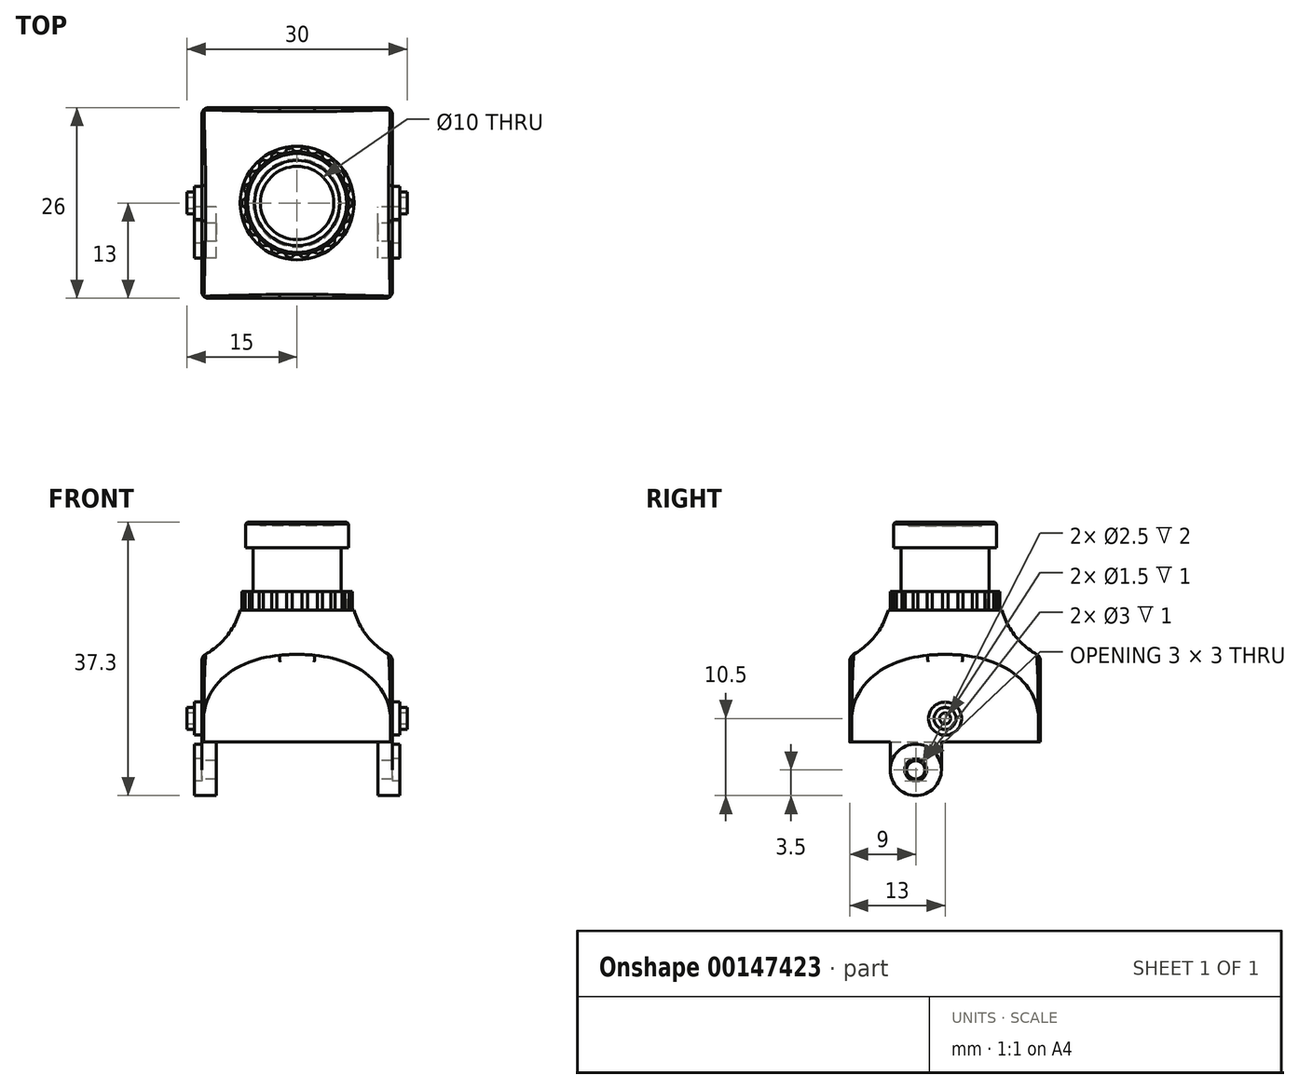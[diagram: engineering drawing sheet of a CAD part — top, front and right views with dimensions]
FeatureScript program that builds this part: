
annotation { "Feature Type Name" : "Feature", "Feature Type Description" : "" }
export const myFeature = defineFeature(function(context is Context, id is Id, definition is map)
    precondition{}
    {
        {
            var Q0;
            Q0=qCreatedBy(makeId("Front.planeOp"),FACE);
            var sketch = newSketch(context, id + "F0", { "sketchPlane" : qUnion([Q0])});
            skLineSegment(sketch, "E0", {"start": v(0, 83.46) * mm, "end": v(0, 0) * mm, "construction": true});
            skLineSegment(sketch, "E1", {"start": v(5, 30) * mm, "end": v(7, 30) * mm});
            skLineSegment(sketch, "E2", {"start": v(7, 30) * mm, "end": v(7, 26.5) * mm});
            skLineSegment(sketch, "E3", {"start": v(7, 26.5) * mm, "end": v(6, 26.5) * mm});
            skLineSegment(sketch, "E4", {"start": v(6, 26.5) * mm, "end": v(6, 20.5) * mm});
            skLineSegment(sketch, "E5", {"start": v(6, 20.5) * mm, "end": v(7.5, 20.5) * mm});
            skLineSegment(sketch, "E6", {"start": v(7.5, 20.5) * mm, "end": v(7.5, 18) * mm});
            skLineSegment(sketch, "E7", {"start": v(7.75, 18) * mm, "end": v(7.5, 18) * mm});
            skLineSegment(sketch, "E8", {"start": v(18, 3) * mm, "end": v(18, 0) * mm});
            skLineSegment(sketch, "E9", {"start": v(18, 0) * mm, "end": v(0, 0) * mm});
            skArc(sketch, "E10", {"start": v(7.75, 18) * mm, "mid": v(9.59, 14.4) * mm, "end": v(12.7, 11.83) * mm});
            skArc(sketch, "E11", {"start": v(18, 3) * mm, "mid": v(16.57, 8.15) * mm, "end": v(12.7, 11.83) * mm});
            skLineSegment(sketch, "E12", {"start": v(5, 30) * mm, "end": v(5, 29.5) * mm});
            skLineSegment(sketch, "E13", {"start": v(0, 29.36) * mm, "end": v(0, 0) * mm});
            skLineSegment(sketch, "E14", {"start": v(0, 29.86) * mm, "end": v(0, 29.36) * mm});
            skArc(sketch, "E15", {"start": v(5, 29.5) * mm, "mid": v(2.5, 29.77) * mm, "end": v(0, 29.86) * mm});
            skSolve(sketch);
        }
        {
            var Q0;
            Q0=makeQuery(id+"F0.imprint","IMPRINT",FACE,{"disambiguationData":[TD([[makeQuery(id+"F0.imprint","IMPRINT",EDGE,{"derivedFrom":sQuery(id+"F0.wireOp",EDGE,"E1")}),-1.0]])]});
            var Q1;
            Q1=sQuery(id+"F0.wireOp",EDGE,"E0");
            revolve(context, id + "F1", {"entities" : qUnion([Q0]), "axis" : qUnion([Q1]), "revolveType" : RevolveType.FULL});
        }
        {
            var Q0;
            Q0=makeQuery(id+"F1.opRevolve","SWEPT_FACE",FACE,{"disambiguationData":[OSD([sQuery(id+"F0.wireOp",EDGE,"E9")])]});
            var sketch = newSketch(context, id + "F2", { "sketchPlane" : qUnion([Q0])});
            skLineSegment(sketch, "E16.bottom", {"start": v(-13, 13) * mm, "end": v(13, 13) * mm});
            skLineSegment(sketch, "E16.top", {"start": v(-13, -13) * mm, "end": v(13, -13) * mm});
            skLineSegment(sketch, "E16.left", {"start": v(-13, 13) * mm, "end": v(-13, -13) * mm});
            skLineSegment(sketch, "E16.right", {"start": v(13, 13) * mm, "end": v(13, -13) * mm});
            skCircle(sketch, "E17", {"center": v(0, 0) * mm, "radius": 20 * mm});
            skSolve(sketch);
        }
        {
            var Q0;
            Q0=qSketchRegion(id+"F2",true);
            extrude(context, id + "F3", {"entities" : qUnion([Q0]), "operationType" : NewBodyOperationType.REMOVE, "oppositeDirection" : true, "depth" : 15 * mm});
        }
        {
            var Q0;
            Q0=makeQuery(id+"F3.boolean.opBoolean","INTERSECT",EDGE,{"disambiguationData":[OD(1.0)],"derivedFrom":[makeQuery(id+"F1.opRevolve","SWEPT_FACE",FACE,{"disambiguationData":[OSD([sQuery(id+"F0.wireOp",EDGE,"E8")])]}),makeQuery(id+"F3.opExtrude","SWEPT_FACE",FACE,{"disambiguationData":[OSD([sQuery(id+"F2.wireOp",EDGE,"E16.left")])]})]});
            var Q1;
            Q1=makeQuery(id+"F3.boolean.opBoolean","INTERSECT",EDGE,{"disambiguationData":[OD(1.0)],"derivedFrom":[makeQuery(id+"F1.opRevolve","SWEPT_FACE",FACE,{"disambiguationData":[OSD([sQuery(id+"F0.wireOp",EDGE,"E11")])]}),makeQuery(id+"F3.opExtrude","SWEPT_FACE",FACE,{"disambiguationData":[OSD([sQuery(id+"F2.wireOp",EDGE,"E16.left")])]})]});
            var Q2;
            Q2=makeQuery(id+"F3.boolean.opBoolean","INTERSECT",EDGE,{"derivedFrom":[makeQuery(id+"F1.opRevolve","SWEPT_FACE",FACE,{"disambiguationData":[OSD([sQuery(id+"F0.wireOp",EDGE,"E10")])]}),makeQuery(id+"F3.opExtrude","SWEPT_FACE",FACE,{"disambiguationData":[OSD([sQuery(id+"F2.wireOp",EDGE,"E16.left")])]})]});
            var Q3;
            Q3=makeQuery(id+"F3.boolean.opBoolean","INTERSECT",EDGE,{"disambiguationData":[OD(0.0)],"derivedFrom":[makeQuery(id+"F1.opRevolve","SWEPT_FACE",FACE,{"disambiguationData":[OSD([sQuery(id+"F0.wireOp",EDGE,"E11")])]}),makeQuery(id+"F3.opExtrude","SWEPT_FACE",FACE,{"disambiguationData":[OSD([sQuery(id+"F2.wireOp",EDGE,"E16.left")])]})]});
            var Q4;
            Q4=makeQuery(id+"F3.boolean.opBoolean","INTERSECT",EDGE,{"disambiguationData":[OD(0.0)],"derivedFrom":[makeQuery(id+"F1.opRevolve","SWEPT_FACE",FACE,{"disambiguationData":[OSD([sQuery(id+"F0.wireOp",EDGE,"E8")])]}),makeQuery(id+"F3.opExtrude","SWEPT_FACE",FACE,{"disambiguationData":[OSD([sQuery(id+"F2.wireOp",EDGE,"E16.left")])]})]});
            var Q5;
            Q5=makeQuery(id+"F3.boolean.opBoolean","INTERSECT",EDGE,{"disambiguationData":[OD(0.0)],"derivedFrom":[makeQuery(id+"F1.opRevolve","SWEPT_FACE",FACE,{"disambiguationData":[OSD([sQuery(id+"F0.wireOp",EDGE,"E8")])]}),makeQuery(id+"F3.opExtrude","SWEPT_FACE",FACE,{"disambiguationData":[OSD([sQuery(id+"F2.wireOp",EDGE,"E16.top")])]})]});
            var Q6;
            Q6=makeQuery(id+"F3.boolean.opBoolean","INTERSECT",EDGE,{"disambiguationData":[OD(1.0)],"derivedFrom":[makeQuery(id+"F1.opRevolve","SWEPT_FACE",FACE,{"disambiguationData":[OSD([sQuery(id+"F0.wireOp",EDGE,"E8")])]}),makeQuery(id+"F3.opExtrude","SWEPT_FACE",FACE,{"disambiguationData":[OSD([sQuery(id+"F2.wireOp",EDGE,"E16.right")])]})]});
            var Q7;
            Q7=makeQuery(id+"F3.boolean.opBoolean","INTERSECT",EDGE,{"disambiguationData":[OD(1.0)],"derivedFrom":[makeQuery(id+"F1.opRevolve","SWEPT_FACE",FACE,{"disambiguationData":[OSD([sQuery(id+"F0.wireOp",EDGE,"E8")])]}),makeQuery(id+"F3.opExtrude","SWEPT_FACE",FACE,{"disambiguationData":[OSD([sQuery(id+"F2.wireOp",EDGE,"E16.bottom")])]})]});
            fillet(context, id + "F4", {"entities" : qUnion([Q0, Q1, Q2, Q3, Q4, Q5, Q6, Q7]), "radius" : 1 * mm, "tangentPropagation" : true, "allowEdgeOverflow" : false});
        }
        {
            var Q0;
            Q0=makeQuery(id+"F1.opRevolve","SWEPT_FACE",FACE,{"disambiguationData":[OSD([sQuery(id+"F0.wireOp",EDGE,"E5")])]});
            var sketch = newSketch(context, id + "F5", { "sketchPlane" : qUnion([Q0])});
            skCircle(sketch, "E18", {"center": v(0, 7.75) * mm, "radius": 0.75 * mm});
            skCircle(sketch, "E19.1.0", {"center": v(-2.18, 7.44) * mm, "radius": 0.75 * mm});
            skCircle(sketch, "E19.2.0", {"center": v(-4.19, 6.52) * mm, "radius": 0.75 * mm});
            skCircle(sketch, "E19.3.0", {"center": v(-5.86, 5.08) * mm, "radius": 0.75 * mm});
            skCircle(sketch, "E19.4.0", {"center": v(-7.05, 3.22) * mm, "radius": 0.75 * mm});
            skCircle(sketch, "E19.5.0", {"center": v(-7.67, 1.1) * mm, "radius": 0.75 * mm});
            skCircle(sketch, "E19.6.0", {"center": v(-7.67, -1.1) * mm, "radius": 0.75 * mm});
            skCircle(sketch, "E19.7.0", {"center": v(-7.05, -3.22) * mm, "radius": 0.75 * mm});
            skCircle(sketch, "E19.8.0", {"center": v(-5.86, -5.08) * mm, "radius": 0.75 * mm});
            skCircle(sketch, "E19.9.0", {"center": v(-4.19, -6.52) * mm, "radius": 0.75 * mm});
            skCircle(sketch, "E19.10.0", {"center": v(-2.18, -7.44) * mm, "radius": 0.75 * mm});
            skCircle(sketch, "E19.11.0", {"center": v(0, -7.75) * mm, "radius": 0.75 * mm});
            skCircle(sketch, "E19.12.0", {"center": v(2.18, -7.44) * mm, "radius": 0.75 * mm});
            skCircle(sketch, "E19.13.0", {"center": v(4.19, -6.52) * mm, "radius": 0.75 * mm});
            skCircle(sketch, "E19.14.0", {"center": v(5.86, -5.08) * mm, "radius": 0.75 * mm});
            skCircle(sketch, "E19.15.0", {"center": v(7.05, -3.22) * mm, "radius": 0.75 * mm});
            skCircle(sketch, "E19.16.0", {"center": v(7.67, -1.1) * mm, "radius": 0.75 * mm});
            skCircle(sketch, "E19.17.0", {"center": v(7.67, 1.1) * mm, "radius": 0.75 * mm});
            skCircle(sketch, "E19.18.0", {"center": v(7.05, 3.22) * mm, "radius": 0.75 * mm});
            skCircle(sketch, "E19.19.0", {"center": v(5.86, 5.08) * mm, "radius": 0.75 * mm});
            skCircle(sketch, "E19.20.0", {"center": v(4.19, 6.52) * mm, "radius": 0.75 * mm});
            skCircle(sketch, "E19.21.0", {"center": v(2.18, 7.44) * mm, "radius": 0.75 * mm});
            skPoint(sketch, "E19.center", {"position": v(0, 0) * mm});
            skCircle(sketch, "E20", {"center": v(0, 0) * mm, "radius": 7.75 * mm, "construction": true});
            skLineSegment(sketch, "E21", {"start": v(0, 7.75) * mm, "end": v(0, 0) * mm, "construction": true});
            skLineSegment(sketch, "E22", {"start": v(0, 0) * mm, "end": v(2.18, 7.44) * mm, "construction": true});
            skSolve(sketch);
        }
        {
            var Q0;
            Q0=qSketchRegion(id+"F5",true);
            extrude(context, id + "F6", {"entities" : qUnion([Q0]), "operationType" : NewBodyOperationType.REMOVE, "oppositeDirection" : true, "depth" : 2.5 * mm});
        }
        {
            var Q0;
            Q0=makeQuery(id+"F1.opRevolve","SWEPT_EDGE",EDGE,{"disambiguationData":[OSD([sQuery(id+"F0.wireOp",EDGE,"E1"),sQuery(id+"F0.wireOp",EDGE,"E2")])]});
            chamfer(context, id + "F7", {"entities" : qUnion([Q0]), "width" : 0.25 * mm, "tangentPropagation" : true});
        }
        {
            var Q0;
            Q0=makeQuery(id+"F1.opRevolve","SWEPT_EDGE",EDGE,{"disambiguationData":[OSD([sQuery(id+"F0.wireOp",EDGE,"E1"),sQuery(id+"F0.wireOp",EDGE,"E12")])]});
            chamfer(context, id + "F8", {"entities" : qUnion([Q0]), "chamferType" : ChamferType.TWO_OFFSETS, "width1" : 0.4 * mm, "oppositeDirection" : false, "width2" : 0.8 * mm, "tangentPropagation" : true});
        }
        {
            var Q0;
            Q0=qCreatedBy(makeId("Right.planeOp"),FACE);
            var sketch = newSketch(context, id + "F9", { "sketchPlane" : qUnion([Q0])});
            skCircle(sketch, "E23", {"center": v(0, 3.2) * mm, "radius": 2.25 * mm});
            skSolve(sketch);
        }
        {
            var Q0;
            Q0=qSketchRegion(id+"F9",true);
            extrude(context, id + "F10", {"entities" : qUnion([Q0]), "operationType" : NewBodyOperationType.ADD, "endBound" : BoundingType.SYMMETRIC, "depth" : 28 * mm});
        }
        {
            var Q0;
            Q0=qCreatedBy(makeId("Right.planeOp"),FACE);
            var sketch = newSketch(context, id + "F11", { "sketchPlane" : qUnion([Q0])});
            skCircle(sketch, "E24", {"center": v(0, 3.2) * mm, "radius": 1.5 * mm});
            skCircle(sketch, "E25", {"center": v(0, 3.2) * mm, "radius": 0.75 * mm});
            skSolve(sketch);
        }
        {
            var Q0;
            Q0=qSketchRegion(id+"F11",true);
            extrude(context, id + "F12", {"entities" : qUnion([Q0]), "operationType" : NewBodyOperationType.ADD, "endBound" : BoundingType.SYMMETRIC, "depth" : 30 * mm});
        }
        {
            var Q0;
            Q0=qCreatedBy(makeId("Right.planeOp"),FACE);
            var sketch = newSketch(context, id + "F13", { "sketchPlane" : qUnion([Q0])});
            skLineSegment(sketch, "E26.bottom", {"start": v(-7.5, 0) * mm, "end": v(-0.5, 0) * mm});
            skLineSegment(sketch, "E26.left", {"start": v(-7.5, 0) * mm, "end": v(-7.5, -3.8) * mm});
            skLineSegment(sketch, "E26.right", {"start": v(-0.5, 0) * mm, "end": v(-0.5, -3.8) * mm});
            skArc(sketch, "E27", {"start": v(-7.5, -3.8) * mm, "mid": v(-4, -7.3) * mm, "end": v(-0.5, -3.8) * mm});
            skCircle(sketch, "E28", {"center": v(-4, -3.8) * mm, "radius": 1.25 * mm});
            skLineSegment(sketch, "E29", {"start": v(-7.5, -3.8) * mm, "end": v(-0.5, -3.8) * mm, "construction": true});
            skSolve(sketch);
        }
        {
            var Q0;
            Q0=qSketchRegion(id+"F13",true);
            extrude(context, id + "F14", {"entities" : qUnion([Q0]), "operationType" : NewBodyOperationType.ADD, "endBound" : BoundingType.SYMMETRIC, "depth" : 26 * mm});
        }
        {
            var Q0;
            Q0=qCreatedBy(makeId("Right.planeOp"),FACE);
            var sketch = newSketch(context, id + "F15", { "sketchPlane" : qUnion([Q0])});
            skCircle(sketch, "E30", {"center": v(-4, -3.8) * mm, "radius": 3.5 * mm});
            skCircle(sketch, "E31", {"center": v(-4, -3.8) * mm, "radius": 1.5 * mm});
            skSolve(sketch);
        }
        {
            var Q0;
            Q0=qSketchRegion(id+"F15",true);
            extrude(context, id + "F16", {"entities" : qUnion([Q0]), "operationType" : NewBodyOperationType.ADD, "endBound" : BoundingType.SYMMETRIC, "depth" : 28 * mm});
        }
        {
            var Q0;
            Q0=qCreatedBy(makeId("Top.planeOp"),FACE);
            var sketch = newSketch(context, id + "F17", { "sketchPlane" : qUnion([Q0])});
            skLineSegment(sketch, "E32.bottom", {"start": v(-11, -13) * mm, "end": v(11, -13) * mm});
            skLineSegment(sketch, "E32.top", {"start": v(-11, 13) * mm, "end": v(11, 13) * mm});
            skLineSegment(sketch, "E32.left", {"start": v(-11, -13) * mm, "end": v(-11, 13) * mm});
            skLineSegment(sketch, "E32.right", {"start": v(11, -13) * mm, "end": v(11, 13) * mm});
            skSolve(sketch);
        }
        {
            var Q0;
            Q0=qSketchRegion(id+"F17",true);
            extrude(context, id + "F18", {"entities" : qUnion([Q0]), "operationType" : NewBodyOperationType.REMOVE, "oppositeDirection" : true, "depth" : 25 * mm});
        }
    });
